# Revit family: Access_Door-Recessed-Cendrex-Plaster_Bead_Flange-(AHA-PLY)
name_source: partatom
category: Specialty Equipment
revit_build: Autodesk Revit Architecture 2013 (Build: 20130531_2115(x64)
units: mm (PartAtom-declared; Revit-internal decimal feet)

## types (6) — shared parameters
Assembly Code = C1020700
Available Options = http://cendrex.com
Cendrex LEED Ready Program = http://www.cendrex.com
Construction Material = Metal - Cendrex - Stainless Steel
Default Elevation = 0"
Description = Recessed access door with plaster bead flange
Finish = Metal - Cendrex - Powder Coated White
Frame Depth = 2 9/32"
Manufacturer = Cendrex
Model = AHA-PLY
Product Documentation Link = http://www.cendrex.com
Product Page URL = http://cendrex.com
URL = http://www.cendrex.com

## per-type parameters (varying)
| type | Frame Height | Frame Width | Height | Height Calc | Width | Width Calc |
| Custom | 41 1/2" | 41 1/2" | 36" | 36" | 36" | 36" |
| 8 x 8 | 13 1/2" | 13 1/2" | 8" | 8" | 8" | 8" |
| 12 x 12 | 17 1/2" | 17 1/2" | 12" | 12" | 12" | 12" |
| 16 x 16 | 21 1/2" | 21 1/2" | 16" | 16" | 16" | 16" |
| 18 x 18 | 23 1/2" | 23 1/2" | 18" | 18" | 18" | 18" |
| 24 x 24 | 29 1/2" | 29 1/2" | 24" | 24" | 24" | 24" |

## geometry (parser evidence)
native form markers: Blend x18, Sweep x15
no freeform markers — native parametric forms only
